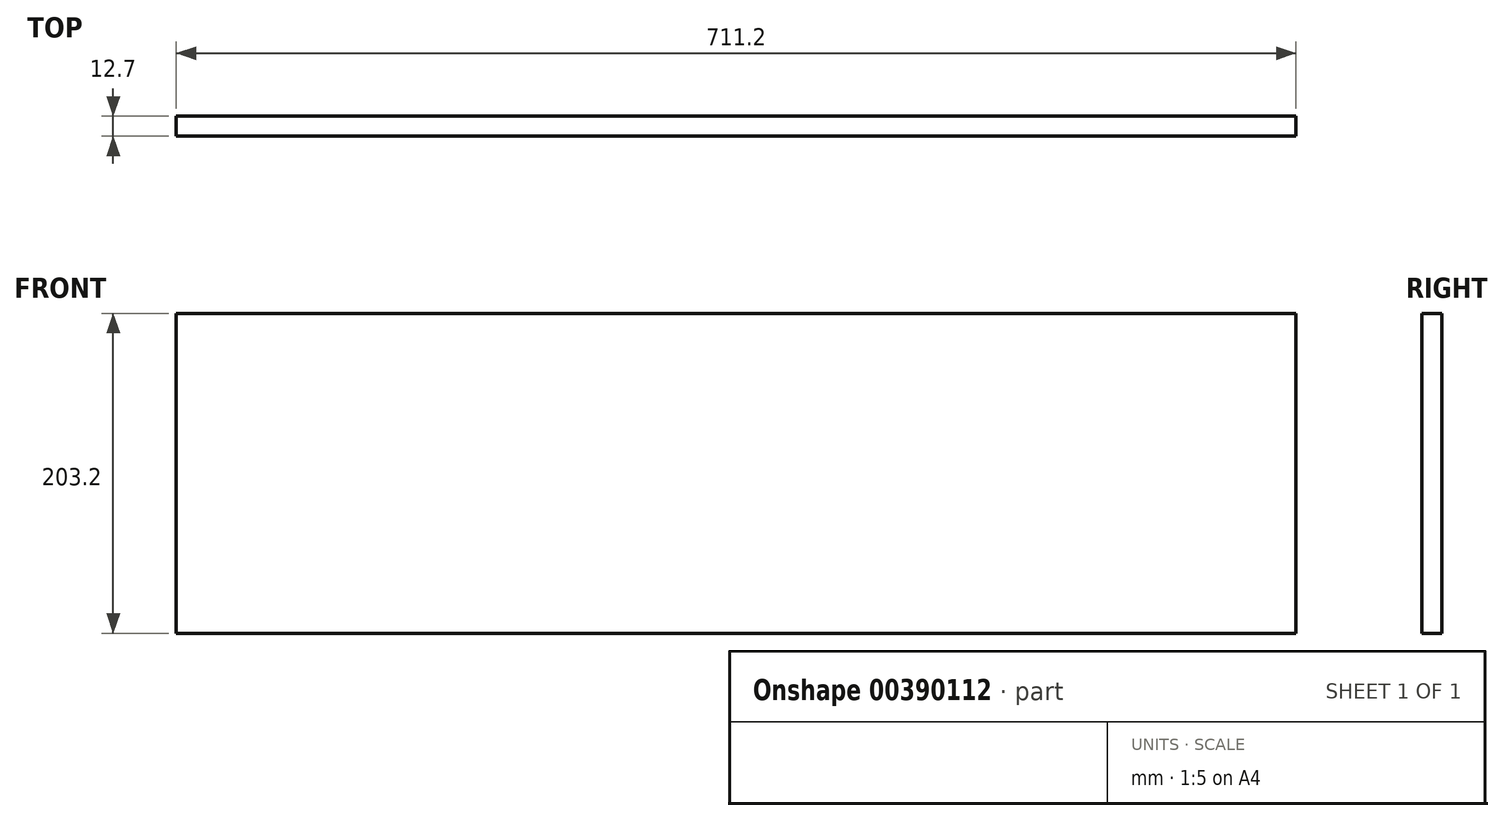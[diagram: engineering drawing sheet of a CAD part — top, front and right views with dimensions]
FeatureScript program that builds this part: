
annotation { "Feature Type Name" : "Feature", "Feature Type Description" : "" }
export const myFeature = defineFeature(function(context is Context, id is Id, definition is map)
    precondition{}
    {
        {
            var Q0;
            Q0=qCreatedBy(makeId("Front.planeOp"),FACE);
            var sketch = newSketch(context, id + "F0", { "sketchPlane" : qUnion([Q0])});
            skLineSegment(sketch, "E0.bottom", {"start": v(0, 203.2) * mm, "end": v(711.2, 203.2) * mm});
            skLineSegment(sketch, "E0.top", {"start": v(0, 0) * mm, "end": v(711.2, 0) * mm});
            skLineSegment(sketch, "E0.left", {"start": v(0, 203.2) * mm, "end": v(0, 0) * mm});
            skLineSegment(sketch, "E0.right", {"start": v(711.2, 203.2) * mm, "end": v(711.2, 0) * mm});
            skSolve(sketch);
        }
        {
            var Q0;
            Q0=makeQuery(id+"F0.imprint","IMPRINT",FACE,{"disambiguationData":[TD([[makeQuery(id+"F0.imprint","IMPRINT",EDGE,{"derivedFrom":sQuery(id+"F0.wireOp",EDGE,"E0.bottom")}),-1.0]])]});
            extrude(context, id + "F1", {"entities" : qUnion([Q0]), "depth" : 12.7 * mm});
        }
    });
